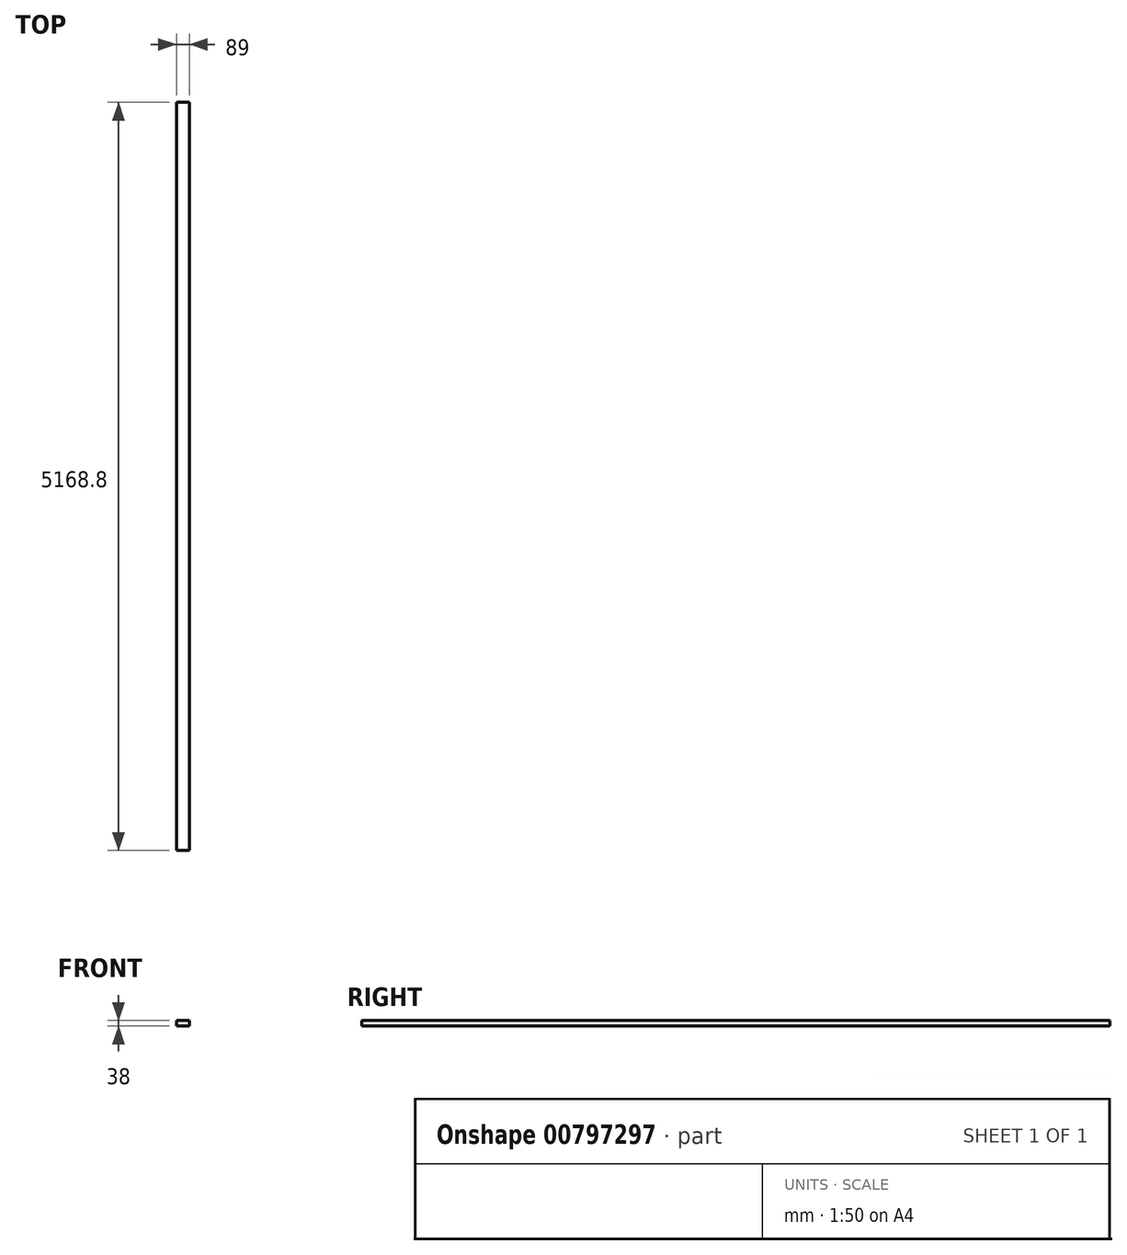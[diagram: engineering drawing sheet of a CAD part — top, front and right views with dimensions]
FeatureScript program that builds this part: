
annotation { "Feature Type Name" : "Feature", "Feature Type Description" : "" }
export const myFeature = defineFeature(function(context is Context, id is Id, definition is map)
    precondition{}
    {
        {
            var Q0;
            Q0=qCreatedBy(makeId("Front.planeOp"),FACE);
            var sketch = newSketch(context, id + "F0", { "sketchPlane" : qUnion([Q0])});
            skLineSegment(sketch, "E0.bottom", {"start": v(44.5, 19) * mm, "end": v(-44.5, 19) * mm});
            skLineSegment(sketch, "E0.top", {"start": v(44.5, -19) * mm, "end": v(-44.5, -19) * mm});
            skLineSegment(sketch, "E0.left", {"start": v(44.5, 19) * mm, "end": v(44.5, -19) * mm});
            skLineSegment(sketch, "E0.right", {"start": v(-44.5, 19) * mm, "end": v(-44.5, -19) * mm});
            skPoint(sketch, "E0.middle", {"position": v(0, 0) * mm});
            skSolve(sketch);
        }
        {
            var Q0;
            Q0=qSketchRegion(id+"F0",true);
            extrude(context, id + "F1", {"entities" : qUnion([Q0]), "depth" : 5168.8 * mm, "offsetDistance" : 25 * mm, "symmetric" : true});
        }
    });
